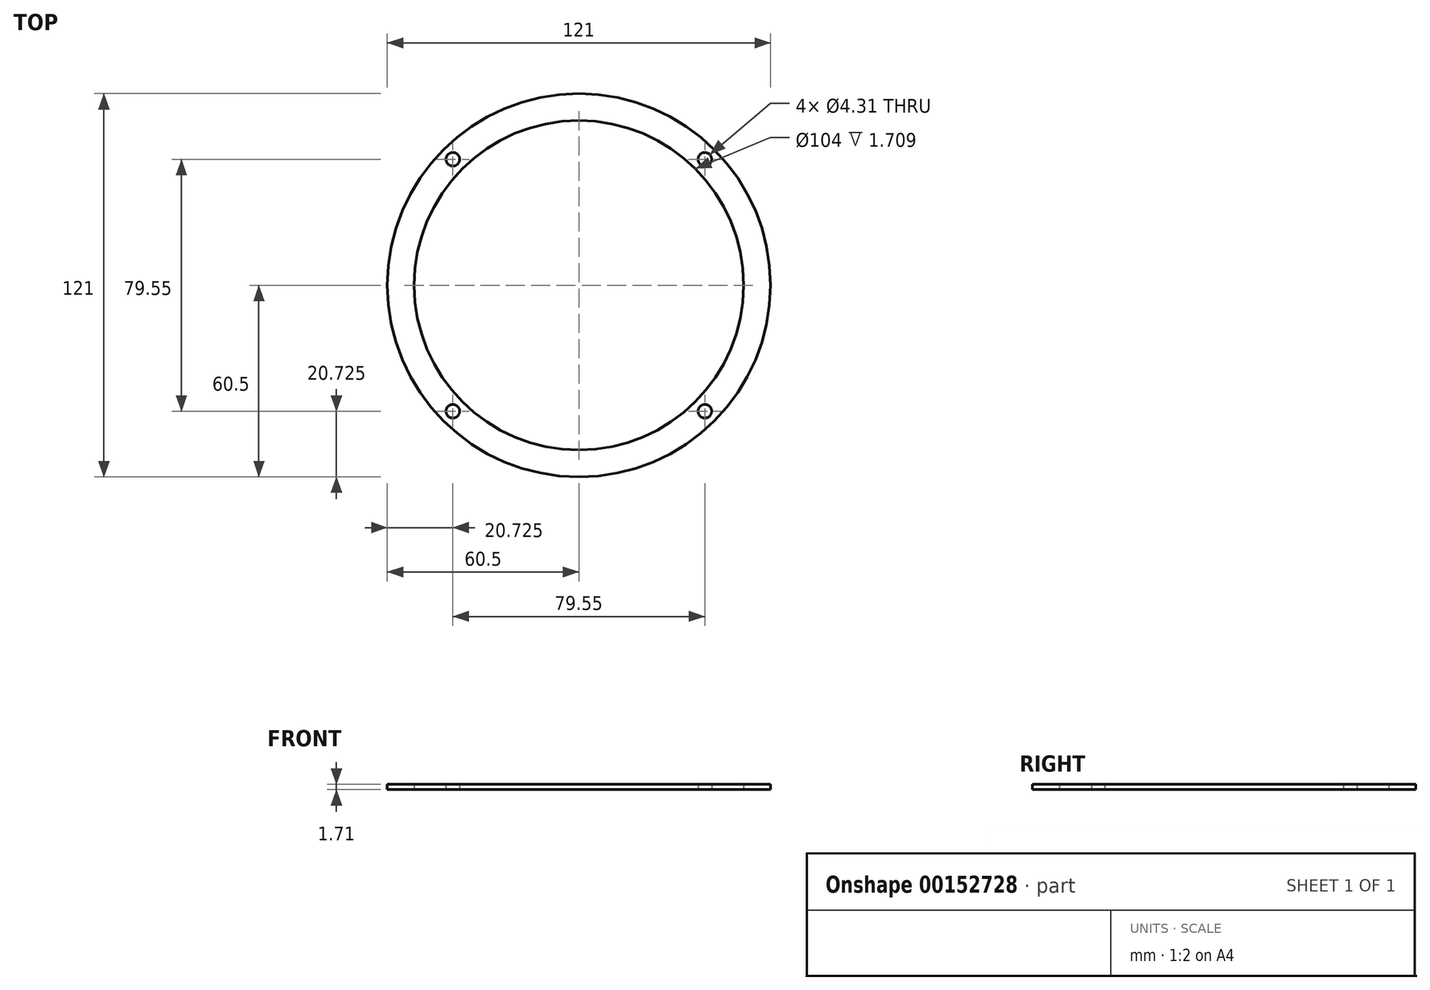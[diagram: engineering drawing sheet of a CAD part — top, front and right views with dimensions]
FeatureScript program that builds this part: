
annotation { "Feature Type Name" : "Feature", "Feature Type Description" : "" }
export const myFeature = defineFeature(function(context is Context, id is Id, definition is map)
    precondition{}
    {
        {
            var Q0;
            Q0=qCreatedBy(makeId("Top.planeOp"),FACE);
            var sketch = newSketch(context, id + "F0", { "sketchPlane" : qUnion([Q0])});
            skCircle(sketch, "E0", {"center": v(0, 0) * mm, "radius": 52 * mm});
            skCircle(sketch, "E1", {"center": v(0, 0) * mm, "radius": 60.5 * mm});
            skCircle(sketch, "E2", {"center": v(-39.77, 39.77) * mm, "radius": 4.25 * mm, "construction": true});
            skLineSegment(sketch, "E3.bottom", {"start": v(-39.77, 39.77) * mm, "end": v(39.77, 39.77) * mm, "construction": true});
            skLineSegment(sketch, "E3.top", {"start": v(-39.77, -39.77) * mm, "end": v(39.77, -39.77) * mm, "construction": true});
            skLineSegment(sketch, "E3.left", {"start": v(-39.77, 39.77) * mm, "end": v(-39.77, -39.77) * mm, "construction": true});
            skLineSegment(sketch, "E3.right", {"start": v(39.77, 39.77) * mm, "end": v(39.77, -39.77) * mm, "construction": true});
            skCircle(sketch, "E4", {"center": v(-39.77, 39.77) * mm, "radius": 2.15 * mm});
            skCircle(sketch, "E5", {"center": v(-39.77, -39.77) * mm, "radius": 2.15 * mm});
            skCircle(sketch, "E6", {"center": v(39.77, -39.77) * mm, "radius": 2.15 * mm});
            skCircle(sketch, "E7", {"center": v(39.77, 39.77) * mm, "radius": 2.15 * mm});
            skSolve(sketch);
        }
        {
            var Q0;
            Q0=qSketchRegion(id+"F0",true);
            extrude(context, id + "F1", {"entities" : qUnion([Q0]), "depth" : 1.7 * mm});
        }
    });
